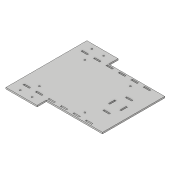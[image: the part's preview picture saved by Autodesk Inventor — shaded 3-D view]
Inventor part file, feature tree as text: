
AUTODESK INVENTOR PART (.ipt)
format: ipt  version: 2017 (Build 210142000, 142)  size: 228,352 bytes
history: native  units: in
note: dims shown in document units (in); Inventor stores cm internally (conversion verified against a paired STEP export)
features: extrude x6, sketch x6
ambient origin geometry x8: Origin, YZ Plane, XZ Plane, XY Plane, X Axis, Y Axis, Z Axis, Center Point
bodies: Solid1 (feature_tree)
feature tree (12):
  extrude  "Extrusion1"  Depth=7.0in
  extrude  "Extrusion2"  Depth=0.115in
  extrude  "Extrusion3"  Depth=1.9685in
  extrude  "Extrusion4"  Depth=0.125in
  extrude  "Extrusion5"  Depth=0.125in
  extrude  "Extrusion6"  Depth=0.115in
  sketch  "Sketch1"  dims[d0=5.0in d1=7.0in]
  sketch  "Sketch2"  dims[d6=0.115in d7=0.0in d8=3.937in]
  sketch  "Sketch4"  dims[d9=3.937in d10=1.9685in]
  sketch  "Sketch5"  dims[d11=2.375in d12=0.125in]
  sketch  "Sketch6"  dims[d13=0.125in d14=0.125in]
  sketch  "Sketch7"  dims[d15=0.125in d16=0.14in d17=0.14in d18=0.14in d19=0.14in d20=0.14in d21=0.14in d22=0.14in d23=0.14in d24=1.0in d25=0.0in d26=0.11in d27=0.11in d28=0.115in d29=0.5in d30=0.5in d31=0.5in d32=0.115in d33=0.5in d34=2.3622in d36=1.0in d37=0.3937in d39=1.0in d41=1.0in d42=0.0in d43=2.5in d44=0.75in d45=2.5in d46=0.75in d47=0.0in d48=0.115in d49=0.0in d50=0.125in d51=0.375in d52=0.375in d53=0.95in d54=0.95in d55=0.375in d56=0.375in d57=0.125in d58=0.125in d59=0.125in d61=0.775in d62=0.115in d63=0.0in d64=0.0in d65=0.775in d66=1.7in d67=0.5in d68=0.835in d69=0.11in d70=0.11in d71=2.0in d72=0.5in d73=0.25in d74=0.8in d75=0.11in d76=0.11in d77=0.15in d78=0.115in d79=0.0in]
